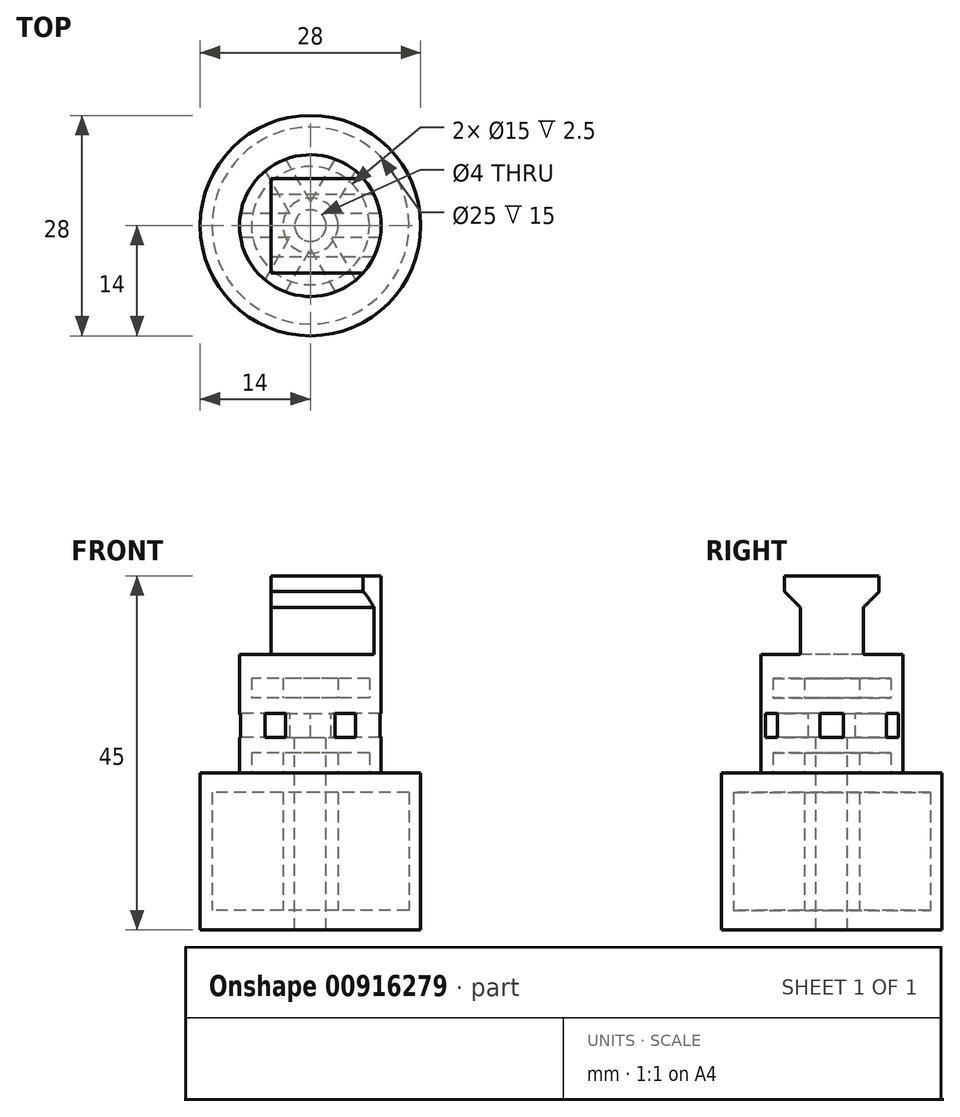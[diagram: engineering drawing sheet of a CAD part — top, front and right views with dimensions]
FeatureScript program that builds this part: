
annotation { "Feature Type Name" : "Feature", "Feature Type Description" : "" }
export const myFeature = defineFeature(function(context is Context, id is Id, definition is map)
    precondition{}
    {
        {
            var Q0;
            Q0=qCreatedBy(makeId("Top.planeOp"),FACE);
            var sketch = newSketch(context, id + "F0", { "sketchPlane" : qUnion([Q0])});
            skCircle(sketch, "E0", {"center": v(0, 0) * mm, "radius": 2 * mm});
            skCircle(sketch, "E1", {"center": v(0, 0) * mm, "radius": 14 * mm});
            skCircle(sketch, "E2", {"center": v(0, 0) * mm, "radius": 3.5 * mm});
            skCircle(sketch, "E3", {"center": v(0, 0) * mm, "radius": 12.5 * mm});
            skSolve(sketch);
        }
        {
            var Q0;
            Q0 = qSketchRegion(id + "F0", true);
            var Q1;
            Q1=makeQuery(id+"F0.imprint","IMPRINT",FACE,{"disambiguationData":[TD([[makeQuery(id+"F0.imprint","IMPRINT",EDGE,{"derivedFrom":sQuery(id+"F0.wireOp",EDGE,"E2")}),-1.0]])]});
            var Q2;
            Q2=makeQuery(id+"F0.imprint","IMPRINT",FACE,{"disambiguationData":[TD([[makeQuery(id+"F0.imprint","IMPRINT",EDGE,{"derivedFrom":sQuery(id+"F0.wireOp",EDGE,"E0")}),-1.0]])]});
            extrude(context, id + "F1", {"entities" : qUnion([Q0, Q1, Q2]), "oppositeDirection" : true, "depth" : 2.5 * mm, "offsetDistance" : 25 * mm});
        }
        {
            var Q0;
            Q0=makeQuery(id+"F0.imprint","IMPRINT",FACE,{"disambiguationData":[TD([[makeQuery(id+"F0.imprint","IMPRINT",EDGE,{"derivedFrom":sQuery(id+"F0.wireOp",EDGE,"E1")}),1.0]])]});
            var Q1;
            Q1=makeQuery(id+"F0.imprint","IMPRINT",FACE,{"disambiguationData":[TD([[makeQuery(id+"F0.imprint","IMPRINT",EDGE,{"derivedFrom":sQuery(id+"F0.wireOp",EDGE,"E0")}),-1.0]])]});
            extrude(context, id + "F2", {"entities" : qUnion([Q0, Q1]), "operationType" : NewBodyOperationType.ADD, "depth" : 15 * mm, "offsetDistance" : 25 * mm});
        }
        {
            var Q0;
            Q0=makeQuery(id+"F2.opExtrude","CAP_FACE",FACE,{"disambiguationData":[OSD([sQuery(id+"F0.wireOp",EDGE,"E0"),sQuery(id+"F0.wireOp",EDGE,"E2")])],"isStart":false});
            var sketch = newSketch(context, id + "F3", { "sketchPlane" : qUnion([Q0])});
            skCircle(sketch, "E4", {"center": v(0, 0) * mm, "radius": 2 * mm});
            skCircle(sketch, "E5", {"center": v(0, 0) * mm, "radius": 14 * mm});
            skSolve(sketch);
        }
        {
            var Q0;
            Q0 = qSketchRegion(id + "F3", true);
            extrude(context, id + "F4", {"entities" : qUnion([Q0]), "operationType" : NewBodyOperationType.ADD, "depth" : 2.5 * mm, "offsetDistance" : 25 * mm});
        }
        {
            var Q0;
            Q0=makeQuery(id+"F4.opExtrude","CAP_FACE",FACE,{"disambiguationData":[OSD([sQuery(id+"F3.wireOp",EDGE,"E4"),sQuery(id+"F3.wireOp",EDGE,"E5")])],"isStart":false});
            var sketch = newSketch(context, id + "F5", { "sketchPlane" : qUnion([Q0])});
            skCircle(sketch, "E6", {"center": v(0, 0) * mm, "radius": 9 * mm});
            skCircle(sketch, "E7", {"center": v(0, 0) * mm, "radius": 7.5 * mm});
            skCircle(sketch, "E8", {"center": v(0, 0) * mm, "radius": 3.5 * mm});
            skSolve(sketch);
        }
        {
            var Q0;
            Q0 = qSketchRegion(id + "F5", true);
            var Q1;
            Q1=makeQuery(id+"F5.imprint","IMPRINT",FACE,{"disambiguationData":[TD([[makeQuery(id+"F5.imprint","IMPRINT",EDGE,{"derivedFrom":sQuery(id+"F5.wireOp",EDGE,"E7")}),1.0]])]});
            var Q2;
            Q2=makeQuery(id+"F5.imprint","IMPRINT",FACE,{"disambiguationData":[TD([[makeQuery(id+"F5.imprint","IMPRINT",EDGE,{"derivedFrom":makeQuery(id+"F4.opExtrude","CAP_EDGE",EDGE,{"disambiguationData":[OSD([sQuery(id+"F3.wireOp",EDGE,"E4")])],"isStart":false})}),1.0]])]});
            var Q3;
            Q3=makeQuery(id+"F5.imprint","IMPRINT",FACE,{"disambiguationData":[TD([[makeQuery(id+"F5.imprint","IMPRINT",EDGE,{"derivedFrom":sQuery(id+"F5.wireOp",EDGE,"E8")}),1.0]])]});
            extrude(context, id + "F6", {"entities" : qUnion([Q0, Q1, Q2, Q3]), "operationType" : NewBodyOperationType.ADD, "depth" : 25 * mm, "offsetDistance" : 25 * mm});
        }
        {
            var Q0;
            Q0=qCreatedBy(makeId("Right.planeOp"),FACE);
            var sketch = newSketch(context, id + "F7", { "sketchPlane" : qUnion([Q0])});
            skLineSegment(sketch, "E9", {"start": v(0, 42.5) * mm, "end": v(6, 42.5) * mm});
            skLineSegment(sketch, "E10", {"start": v(0, 42.5) * mm, "end": v(0, 32.5) * mm});
            skLineSegment(sketch, "E11", {"start": v(0, 32.5) * mm, "end": v(4, 32.5) * mm});
            skLineSegment(sketch, "E12", {"start": v(4, 32.5) * mm, "end": v(4, 40.5) * mm});
            skLineSegment(sketch, "E13", {"start": v(4, 40.5) * mm, "end": v(6, 40.5) * mm});
            skLineSegment(sketch, "E14", {"start": v(6, 40.5) * mm, "end": v(6, 42.5) * mm});
            skLineSegment(sketch, "E15", {"start": v(4, 32.5) * mm, "end": v(9, 32.5) * mm});
            skLineSegment(sketch, "E16", {"start": v(9, 32.5) * mm, "end": v(9, 42.5) * mm});
            skLineSegment(sketch, "E17", {"start": v(9, 42.5) * mm, "end": v(6, 42.5) * mm});
            skLineSegment(sketch, "E18.MirrorCS", {"start": v(-4, 32.5) * mm, "end": v(-4, 40.5) * mm});
            skLineSegment(sketch, "E19.MirrorCS", {"start": v(0, 32.5) * mm, "end": v(-4, 32.5) * mm});
            skLineSegment(sketch, "E20.MirrorCS", {"start": v(0, 42.5) * mm, "end": v(-6, 42.5) * mm});
            skLineSegment(sketch, "E21.MirrorCS", {"start": v(-6, 40.5) * mm, "end": v(-6, 42.5) * mm});
            skLineSegment(sketch, "E22.MirrorCS", {"start": v(-4, 32.5) * mm, "end": v(-9, 32.5) * mm});
            skLineSegment(sketch, "E23.MirrorCS", {"start": v(-9, 32.5) * mm, "end": v(-9, 42.5) * mm});
            skLineSegment(sketch, "E24.MirrorCS", {"start": v(-9, 42.5) * mm, "end": v(-6, 42.5) * mm});
            skLineSegment(sketch, "E25.MirrorCS", {"start": v(-4, 40.5) * mm, "end": v(-6, 40.5) * mm});
            skSolve(sketch);
        }
        {
            var Q0;
            Q0=makeQuery(id+"F7.imprint","IMPRINT",FACE,{"disambiguationData":[TD([[makeQuery(id+"F7.imprint","IMPRINT",EDGE,{"derivedFrom":sQuery(id+"F7.wireOp",EDGE,"E18.MirrorCS")}),1.0]])]});
            var Q1;
            Q1=makeQuery(id+"F7.imprint","IMPRINT",FACE,{"disambiguationData":[TD([[makeQuery(id+"F7.imprint","IMPRINT",EDGE,{"derivedFrom":sQuery(id+"F7.wireOp",EDGE,"E12")}),-1.0]])]});
            extrude(context, id + "F8", {"entities" : qUnion([Q0, Q1]), "operationType" : NewBodyOperationType.REMOVE, "depth" : 25 * mm, "offsetDistance" : 25 * mm, "hasSecondDirection" : true, "secondDirectionOppositeDirection" : true, "secondDirectionDepth" : 25 * mm});
        }
        {
            var Q0;
            Q0=makeQuery(id+"F6.opExtrude","CAP_FACE",FACE,{"disambiguationData":[OSD([sQuery(id+"F5.wireOp",EDGE,"E6")])],"isStart":false});
            var sketch = newSketch(context, id + "F9", { "sketchPlane" : qUnion([Q0])});
            skLineSegment(sketch, "E26.bottom", {"start": v(-13, 7.12) * mm, "end": v(-5, 7.12) * mm});
            skLineSegment(sketch, "E26.top", {"start": v(-13, -7.12) * mm, "end": v(-5, -7.12) * mm});
            skLineSegment(sketch, "E26.left", {"start": v(-13, 7.12) * mm, "end": v(-13, -7.12) * mm});
            skLineSegment(sketch, "E26.right", {"start": v(-5, 7.12) * mm, "end": v(-5, -7.12) * mm});
            skPoint(sketch, "E26.middle", {"position": v(-9, 0) * mm});
            skSolve(sketch);
        }
        {
            var Q0;
            Q0 = qSketchRegion(id + "F9", true);
            extrude(context, id + "F10", {"entities" : qUnion([Q0]), "operationType" : NewBodyOperationType.REMOVE, "oppositeDirection" : true, "depth" : 10 * mm, "offsetDistance" : 25 * mm});
        }
        {
            var Q0;
            Q0=makeQuery(id+"F0.imprint","IMPRINT",FACE,{"disambiguationData":[TD([[makeQuery(id+"F0.imprint","IMPRINT",EDGE,{"derivedFrom":sQuery(id+"F0.wireOp",EDGE,"E0")}),1.0]])]});
            var Q1;
            Q1=sQuery(id+"F0.wireOp",EDGE,"E0");
            extrude(context, id + "F11", {"entities" : qUnion([Q0]), "operationType" : NewBodyOperationType.REMOVE, "surfaceEntities" : qUnion([Q1]), "depth" : 25 * mm, "offsetDistance" : 25 * mm});
        }
        {
            var Q0;
            Q0=makeQuery(id+"F11.boolean.opBoolean","COPY",FACE,{"derivedFrom":makeQuery(id+"F11.opExtrude","CAP_FACE",FACE,{"disambiguationData":[OSD([sQuery(id+"F0.wireOp",EDGE,"E0")])],"isStart":false})});
            var sketch = newSketch(context, id + "F12", { "sketchPlane" : qUnion([Q0])});
            skLineSegment(sketch, "E27.bottom", {"start": v(23.68, -1.5) * mm, "end": v(-23.68, -1.5) * mm});
            skLineSegment(sketch, "E27.top", {"start": v(23.68, 1.5) * mm, "end": v(-23.68, 1.5) * mm});
            skLineSegment(sketch, "E27.left", {"start": v(23.68, -1.5) * mm, "end": v(23.68, 1.5) * mm});
            skLineSegment(sketch, "E27.right", {"start": v(-23.68, -1.5) * mm, "end": v(-23.68, 1.5) * mm});
            skPoint(sketch, "E27.middle", {"position": v(0, 0) * mm});
            skLineSegment(sketch, "E28.1.1", {"start": v(-10.54, 21.26) * mm, "end": v(13.14, -19.76) * mm});
            skLineSegment(sketch, "E28.1.2", {"start": v(-13.14, 19.76) * mm, "end": v(10.54, -21.26) * mm});
            skLineSegment(sketch, "E28.1.3", {"start": v(13.14, -19.76) * mm, "end": v(10.54, -21.26) * mm});
            skLineSegment(sketch, "E28.1.4", {"start": v(-10.54, 21.26) * mm, "end": v(-13.14, 19.76) * mm});
            skLineSegment(sketch, "E28.2.1", {"start": v(-13.14, -19.76) * mm, "end": v(10.54, 21.26) * mm});
            skLineSegment(sketch, "E28.2.2", {"start": v(-10.54, -21.26) * mm, "end": v(13.14, 19.76) * mm});
            skLineSegment(sketch, "E28.2.3", {"start": v(10.54, 21.26) * mm, "end": v(13.14, 19.76) * mm});
            skLineSegment(sketch, "E28.2.4", {"start": v(-13.14, -19.76) * mm, "end": v(-10.54, -21.26) * mm});
            skSolve(sketch);
        }
        {
            var Q0;
            Q0 = qSketchRegion(id + "F12", true);
            extrude(context, id + "F13", {"entities" : qUnion([Q0]), "operationType" : NewBodyOperationType.REMOVE, "depth" : 3 * mm, "offsetDistance" : 25 * mm});
        }
        {
            var Q0;
            Q0=makeQuery(id+"F5.imprint","IMPRINT",FACE,{"disambiguationData":[TD([[makeQuery(id+"F5.imprint","IMPRINT",EDGE,{"derivedFrom":sQuery(id+"F5.wireOp",EDGE,"E7")}),1.0]])]});
            extrude(context, id + "F14", {"entities" : qUnion([Q0]), "operationType" : NewBodyOperationType.REMOVE, "depth" : 2.5 * mm, "offsetDistance" : 25 * mm});
        }
        {
            var Q0;
            Q0=makeQuery(id+"F5.imprint","IMPRINT",FACE,{"disambiguationData":[TD([[makeQuery(id+"F5.imprint","IMPRINT",EDGE,{"derivedFrom":sQuery(id+"F5.wireOp",EDGE,"E7")}),1.0]])]});
            extrude(context, id + "F15", {"entities" : qUnion([Q0]), "operationType" : NewBodyOperationType.REMOVE, "depth" : 12 * mm, "offsetDistance" : 25 * mm, "hasSecondDirection" : true, "secondDirectionOppositeDirection" : false, "secondDirectionDepth" : 9.5 * mm});
        }
        {
            var Q0;
            Q0=makeQuery(id+"F8.boolean.opBoolean","COPY",EDGE,{"derivedFrom":makeQuery(id+"F8.opExtrude","SWEPT_EDGE",EDGE,{"disambiguationData":[OSD([sQuery(id+"F7.wireOp",EDGE,"E18.MirrorCS"),sQuery(id+"F7.wireOp",EDGE,"E25.MirrorCS")])]})});
            var Q1;
            Q1=makeQuery(id+"F8.boolean.opBoolean","COPY",EDGE,{"derivedFrom":makeQuery(id+"F8.opExtrude","SWEPT_EDGE",EDGE,{"disambiguationData":[OSD([sQuery(id+"F7.wireOp",EDGE,"E12"),sQuery(id+"F7.wireOp",EDGE,"E13")])]})});
            chamfer(context, id + "F16", {"entities" : qUnion([Q0, Q1]), "chamferType" : ChamferType.OFFSET_ANGLE, "width" : 2 * mm, "oppositeDirection" : false, "angle" : 45 * degree, "tangentPropagation" : true});
        }
    });
